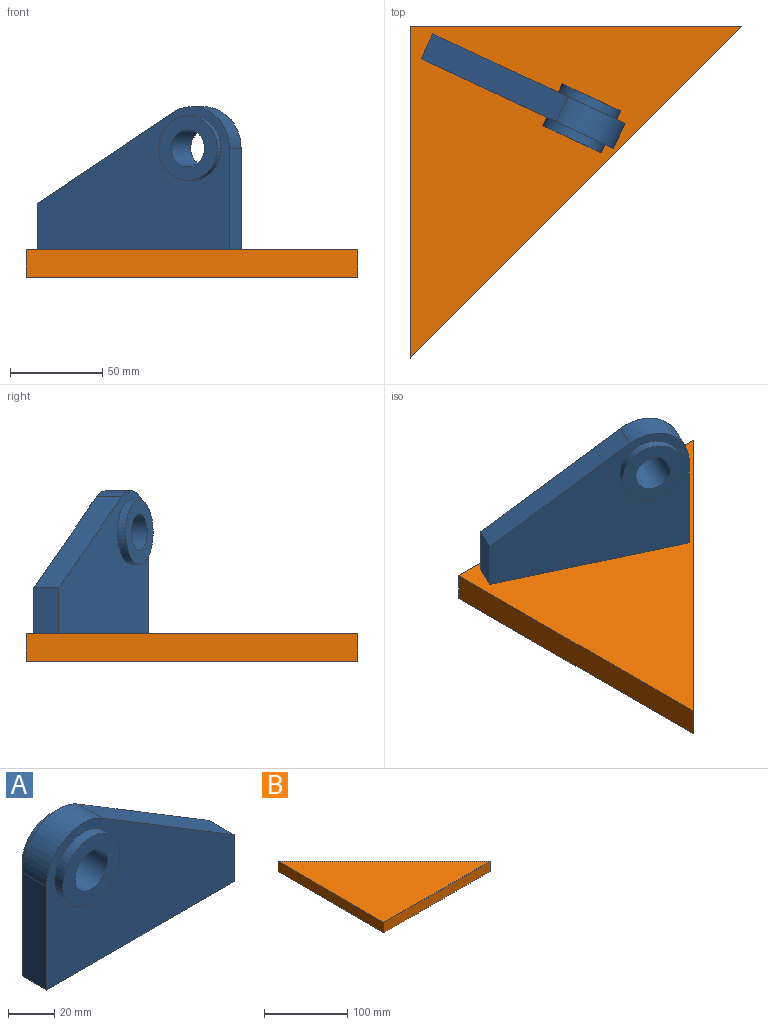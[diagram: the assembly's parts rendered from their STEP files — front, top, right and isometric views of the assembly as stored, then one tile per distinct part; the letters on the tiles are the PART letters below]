
ASSEMBLY  parts=2 mates=1
PART A: 12 faces, bbox 115x25x77.5 mm
  f0: plane 80.8x49.22mm, normal (0.52,0,0.85), area 1419.1mm2, adj f1,f4,f5,f6
  f1: cylinder r=22.5mm len=34.21mm, axis (0,-1,0), area 714.8mm2, adj f0,f2,f5,f6
  f2: plane 55x15mm, normal (-1,0,0), area 825mm2, adj f1,f3,f5,f6
  f3: plane 115x15mm, normal (0,0,-1), area 1725mm2, adj f2,f4,f5,f6
  f4: plane 25x15mm, normal (1,0,0), area 375mm2, adj f0,f3,f5,f6
  f5: plane 115x77.5mm, normal (0,1,0), area 5575.8mm2, adj f0,f1,f2,f3,f4,f10
  f6: plane 115x77.5mm, normal (0,-1,0), area 5575.8mm2, adj f0,f1,f2,f3,f4,f8
  f7: plane 35x35mm, normal (0,-1,0), area 648mm2, adj f8,f9
  f8: cylinder r=17.5mm len=35mm, axis (0,1,0), area 549.8mm2, adj f6,f7
  f9: cylinder r=10mm len=25mm, axis (0,-1,0), area 1570.8mm2, adj f7,f11
  f10: cylinder r=17.5mm len=35mm, axis (0,1,0), area 549.8mm2, adj f5,f11
  f11: plane 35x35mm, normal (0,1,0), area 648mm2, adj f9,f10
PART B: 5 faces, bbox 180x180x15 mm
  f0: plane 180x15mm, normal (-1,0,0), area 2700mm2, adj f1,f2,f3,f4
  f1: plane 180x15mm, normal (0,-1,0), area 2700mm2, adj f0,f2,f3,f4
  f2: plane 180x180mm, normal (0.71,0.71,0), area 3818.4mm2, adj f0,f1,f3,f4
  f3: plane 180x180mm, normal (0,0,1), area 16200mm2, adj f0,f1,f2
  f4: plane 180x180mm, normal (0,0,-1), area 16200mm2, adj f0,f1,f2
PLACE A rot(axis=(0,0,1),155deg) t=(79.42,79.53,78.47)mm
PLACE B rot(axis=(0,0,-1),90deg) t=(-16.81,122.9,8.47)mm
MATE planar A.f3 <-> B.f3  axis (0,0,-1) through (44.53,87.52,23.47)mm
